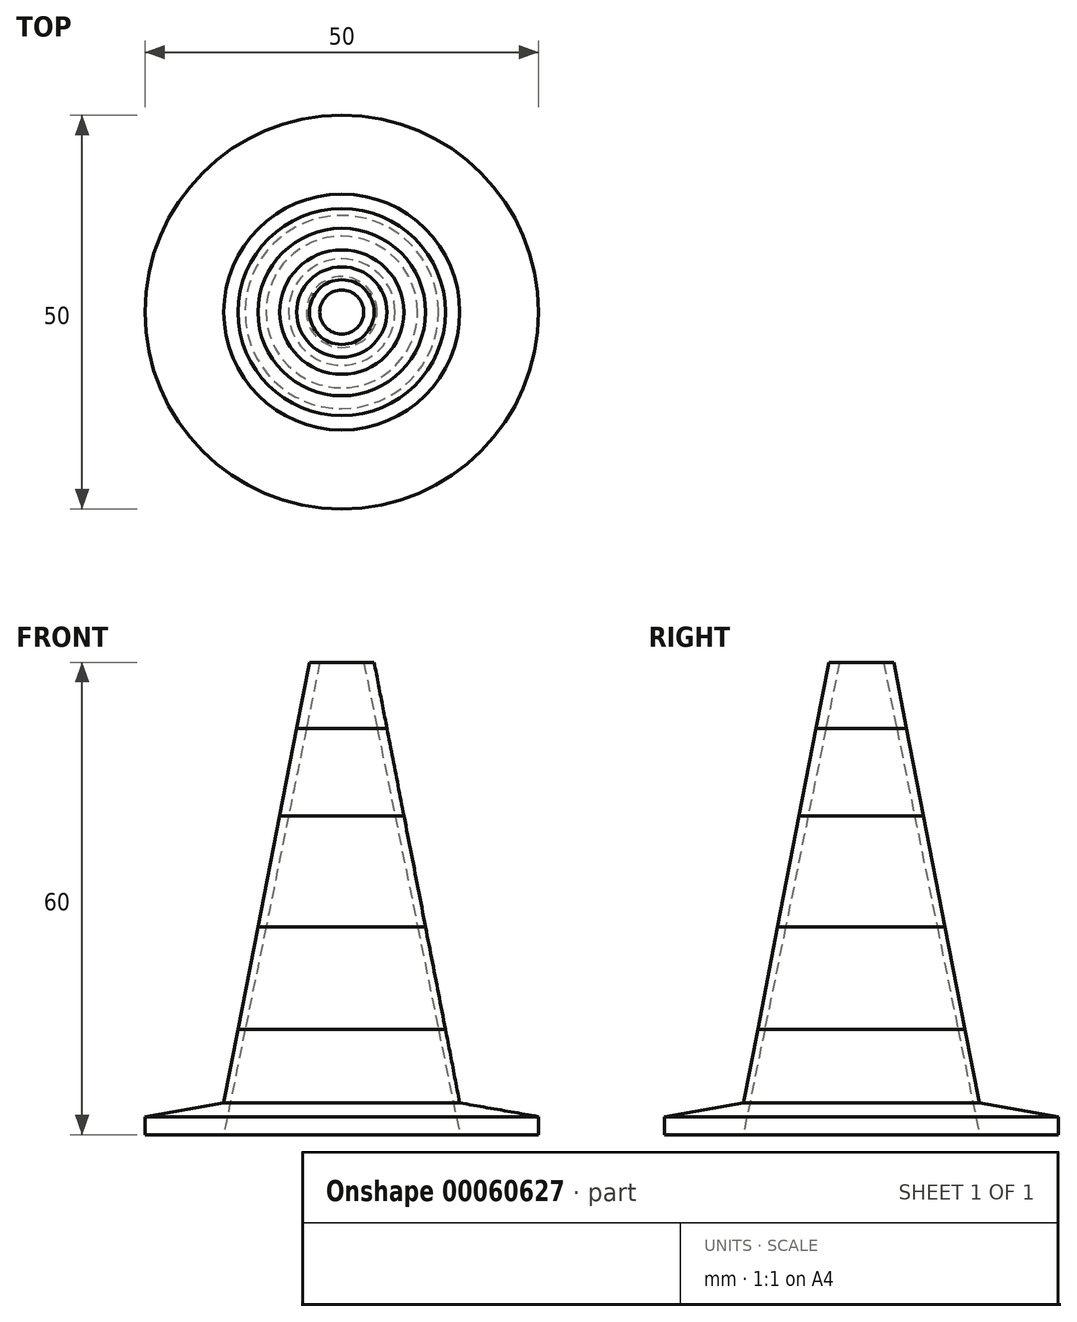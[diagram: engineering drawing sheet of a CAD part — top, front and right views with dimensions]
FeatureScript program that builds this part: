
annotation { "Feature Type Name" : "Feature", "Feature Type Description" : "" }
export const myFeature = defineFeature(function(context is Context, id is Id, definition is map)
    precondition{}
    {
        {
            var Q0;
            Q0=qCreatedBy(makeId("Front.planeOp"),FACE);
            var sketch = newSketch(context, id + "F0", { "sketchPlane" : qUnion([Q0])});
            skLineSegment(sketch, "E0", {"start": v(0, 0) * mm, "end": v(-25, 0) * mm});
            skLineSegment(sketch, "E1", {"start": v(-25, 0) * mm, "end": v(-25, 2.28) * mm});
            skLineSegment(sketch, "E2", {"start": v(-25, 2.28) * mm, "end": v(-14.98, 4.05) * mm});
            skLineSegment(sketch, "E3", {"start": v(-14.98, 4.05) * mm, "end": v(-4.1, 60) * mm});
            skLineSegment(sketch, "E4", {"start": v(-4.1, 60) * mm, "end": v(0, 60) * mm});
            skLineSegment(sketch, "E5", {"start": v(0, 60) * mm, "end": v(0, 0) * mm});
            skLineSegment(sketch, "E6", {"start": v(-13.17, 13.4) * mm, "end": v(0, 13.4) * mm});
            skLineSegment(sketch, "E7", {"start": v(-10.64, 26.4) * mm, "end": v(0, 26.4) * mm});
            skLineSegment(sketch, "E8", {"start": v(-7.9, 40.5) * mm, "end": v(0, 40.5) * mm});
            skLineSegment(sketch, "E9", {"start": v(-5.74, 51.6) * mm, "end": v(0, 51.6) * mm});
            skSolve(sketch);
        }
        {
            var Q0;
            {var subQ0=sQuery(id+"F0.wireOp",EDGE,"E4");Q0=makeQuery(id+"F0.imprint","IMPRINT",FACE,{"disambiguationData":[TD([[makeQuery(id+"F0.imprint","IMPRINT",EDGE,{"derivedFrom":subQ0}),-1.0]])]});}
            var Q1;
            Q1=sQuery(id+"F0.wireOp",EDGE,"E5");
            revolve(context, id + "F1", {"entities" : qUnion([Q0]), "axis" : qUnion([Q1]), "revolveType" : RevolveType.FULL});
        }
        {
            var Q0;
            {var subQ0=sQuery(id+"F0.wireOp",EDGE,"E8");Q0=makeQuery(id+"F0.imprint","IMPRINT",FACE,{"disambiguationData":[TD([[makeQuery(id+"F0.imprint","IMPRINT",EDGE,{"derivedFrom":subQ0}),1.0]])]});}
            var Q1;
            Q1=sQuery(id+"F0.wireOp",EDGE,"E5");
            revolve(context, id + "F2", {"entities" : qUnion([Q0]), "axis" : qUnion([Q1]), "revolveType" : RevolveType.FULL});
        }
        {
            var Q0;
            {var subQ0=sQuery(id+"F0.wireOp",EDGE,"E7");Q0=makeQuery(id+"F0.imprint","IMPRINT",FACE,{"disambiguationData":[TD([[makeQuery(id+"F0.imprint","IMPRINT",EDGE,{"derivedFrom":subQ0}),1.0]])]});}
            var Q1;
            Q1=sQuery(id+"F0.wireOp",EDGE,"E5");
            revolve(context, id + "F3", {"entities" : qUnion([Q0]), "axis" : qUnion([Q1]), "revolveType" : RevolveType.FULL});
        }
        {
            var Q0;
            {var subQ0=sQuery(id+"F0.wireOp",EDGE,"E6");Q0=makeQuery(id+"F0.imprint","IMPRINT",FACE,{"disambiguationData":[TD([[makeQuery(id+"F0.imprint","IMPRINT",EDGE,{"derivedFrom":subQ0}),1.0]])]});}
            var Q1;
            Q1=sQuery(id+"F0.wireOp",EDGE,"E5");
            revolve(context, id + "F4", {"entities" : qUnion([Q0]), "axis" : qUnion([Q1]), "revolveType" : RevolveType.FULL});
        }
        {
            var Q0;
            {var subQ3=sQuery(id+"F0.wireOp",EDGE,"E0");Q0=makeQuery(id+"F0.imprint","IMPRINT",FACE,{"disambiguationData":[TD([[makeQuery(id+"F0.imprint","IMPRINT",EDGE,{"derivedFrom":subQ3}),-1.0]])]});}
            var Q1;
            Q1=sQuery(id+"F0.wireOp",EDGE,"E5");
            revolve(context, id + "F5", {"entities" : qUnion([Q0]), "axis" : qUnion([Q1]), "revolveType" : RevolveType.FULL});
        }
        {
            var Q0;
            Q0=makeQuery(id+"F5.opRevolve","SWEPT_FACE",FACE,{"disambiguationData":[OSD([sQuery(id+"F0.wireOp",EDGE,"E0")])]});
            var sketch = newSketch(context, id + "F6", { "sketchPlane" : qUnion([Q0])});
            skCircle(sketch, "E10", {"center": v(0, 0) * mm, "radius": 15 * mm});
            skSolve(sketch);
        }
        {
            var Q0;
            Q0 = qSketchRegion(id + "F6", true);
            extrude(context, id + "F7", {"entities" : qUnion([Q0]), "operationType" : NewBodyOperationType.REMOVE, "endBound" : BoundingType.THROUGH_ALL, "oppositeDirection" : true, "depth" : 25 * mm, "hasDraft" : true, "draftAngle" : 11.5 * degree, "draftPullDirection" : true});
        }
    });
